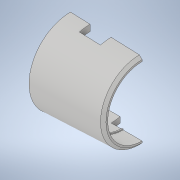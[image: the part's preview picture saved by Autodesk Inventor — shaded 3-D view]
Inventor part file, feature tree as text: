
AUTODESK INVENTOR PART (.ipt)
format: ipt  version: 2020 (Build 240168000, 168)  size: 161,280 bytes
history: native  units: mm
features: sketch x3, extrude x2, revolve x1, chamfer x1
ambient origin geometry x8: Origin, YZ Plane, XZ Plane, XY Plane, X Axis, Y Axis, Z Axis, Center Point
bodies: Solid1 (feature_tree)
feature tree (7):
  revolve  "Revolution1"  [1 undecoded]
  extrude  "Extrusion1"  Depth=200.0mm TaperAngle=0.0deg
  extrude  "Extrusion2"  Depth=11.85mm
  chamfer  "Chamfer1"  Distance=6.0mm
  sketch  "Sketch2"  dims[d2=40.25mm d3=9.7mm]
  sketch  "Sketch3"  dims[d9=270.0deg d17=200.0mm d18=0.0mm]
  sketch  "Sketch4"  dims[d21=11.0mm d23=5.0mm d24=6.0mm d25=11.0mm d27=200.0mm d28=0.0mm d31=1.5mm d32=2.0mm d33=45.0deg d34=0.5mm d36=0.7mm d39=4.0mm d40=2.5mm d41=19.3mm d43=11.85mm d44=11.85mm d45=11.35mm]
note: 1 required parameter value undecoded (feature->parameter linkage not recoverable at this tier; creation-order binding heuristic only, values carry confidence <= 0.55)
